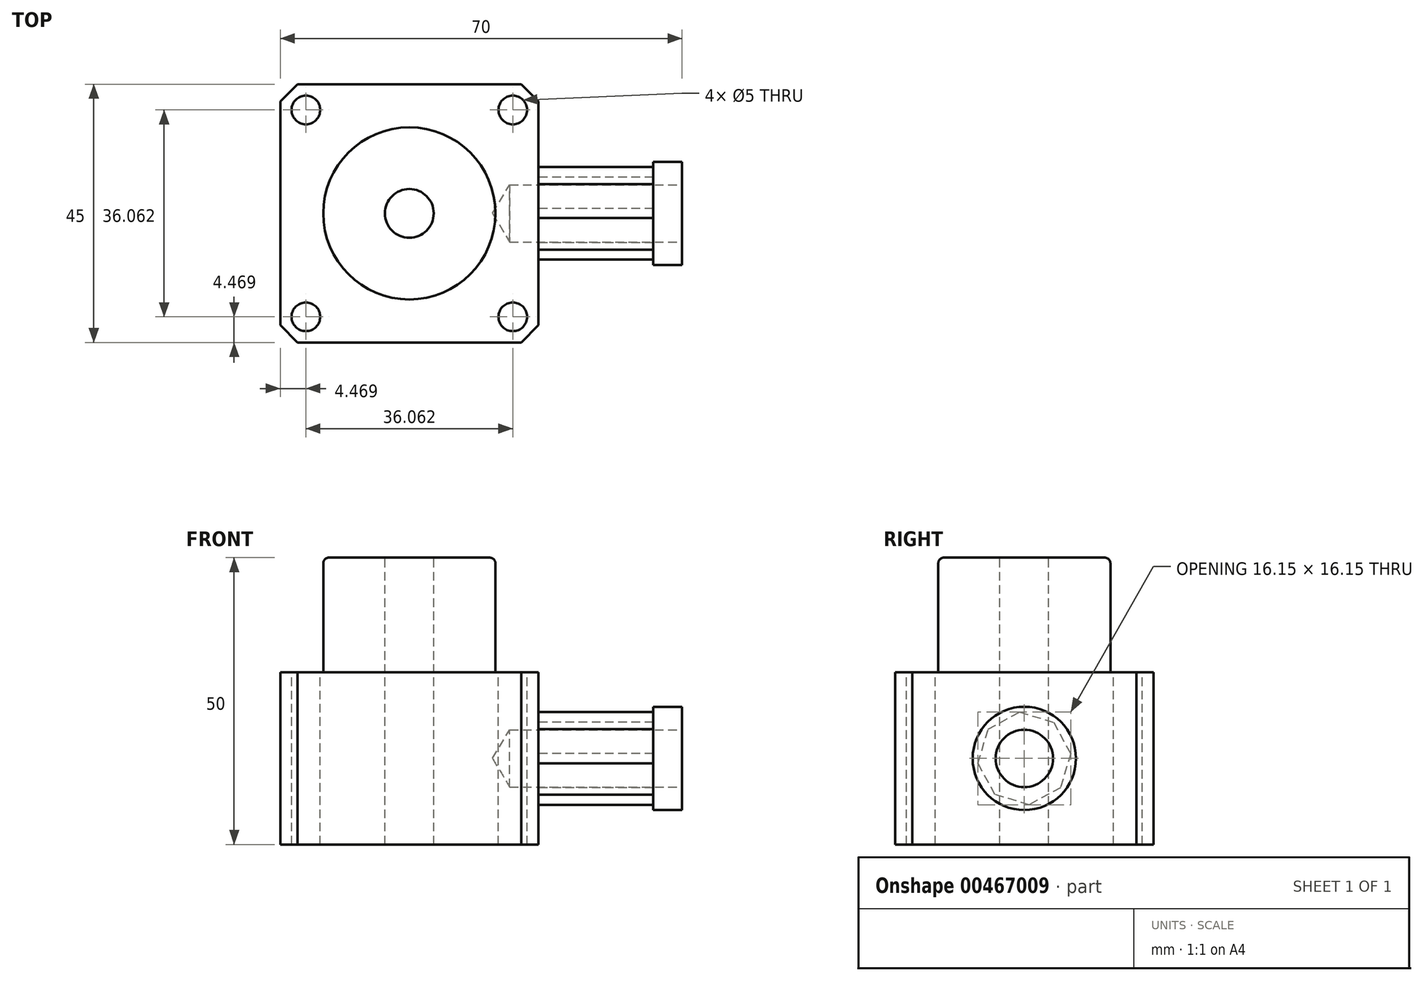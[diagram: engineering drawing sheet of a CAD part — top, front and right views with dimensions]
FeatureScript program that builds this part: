
annotation { "Feature Type Name" : "Feature", "Feature Type Description" : "" }
export const myFeature = defineFeature(function(context is Context, id is Id, definition is map)
    precondition{}
    {
        {
            var Q0;
            Q0=qCreatedBy(makeId("Top.planeOp"),FACE);
            var sketch = newSketch(context, id + "F0", { "sketchPlane" : qUnion([Q0])});
            skLineSegment(sketch, "E0.bottom", {"start": v(0, 0) * mm, "end": v(-45, 0) * mm});
            skLineSegment(sketch, "E0.top", {"start": v(0, -45) * mm, "end": v(-45, -45) * mm});
            skLineSegment(sketch, "E0.left", {"start": v(0, 0) * mm, "end": v(0, -45) * mm});
            skLineSegment(sketch, "E0.right", {"start": v(-45, 0) * mm, "end": v(-45, -45) * mm});
            skSolve(sketch);
        }
        {
            var Q0;
            Q0=makeQuery(id+"F0.imprint","IMPRINT",FACE,{"disambiguationData":[TD([[makeQuery(id+"F0.imprint","IMPRINT",EDGE,{"derivedFrom":sQuery(id+"F0.wireOp",EDGE,"E0.bottom")}),1.0]])]});
            extrude(context, id + "F1", {"entities" : qUnion([Q0]), "depth" : 30 * mm});
        }
        {
            var Q0;
            Q0=makeQuery(id+"F1.opExtrude","SWEPT_EDGE",EDGE,{"disambiguationData":[OSD([sQuery(id+"F0.wireOp",EDGE,"E0.top"),sQuery(id+"F0.wireOp",EDGE,"E0.right")])]});
            var Q1;
            Q1=makeQuery(id+"F1.opExtrude","SWEPT_EDGE",EDGE,{"disambiguationData":[OSD([sQuery(id+"F0.wireOp",EDGE,"E0.top"),sQuery(id+"F0.wireOp",EDGE,"E0.left")])]});
            var Q2;
            Q2=makeQuery(id+"F1.opExtrude","SWEPT_EDGE",EDGE,{"disambiguationData":[OSD([sQuery(id+"F0.wireOp",EDGE,"E0.bottom"),sQuery(id+"F0.wireOp",EDGE,"E0.left")])]});
            var Q3;
            Q3=makeQuery(id+"F1.opExtrude","SWEPT_EDGE",EDGE,{"disambiguationData":[OSD([sQuery(id+"F0.wireOp",EDGE,"E0.bottom"),sQuery(id+"F0.wireOp",EDGE,"E0.right")])]});
            chamfer(context, id + "F2", {"entities" : qUnion([Q0, Q1, Q2, Q3]), "width" : 3 * mm, "tangentPropagation" : true});
        }
        {
            var Q0;
            Q0=makeQuery(id+"F1.opExtrude","CAP_FACE",FACE,{"disambiguationData":[OSD([sQuery(id+"F0.wireOp",EDGE,"E0.bottom"),sQuery(id+"F0.wireOp",EDGE,"E0.top"),sQuery(id+"F0.wireOp",EDGE,"E0.left"),sQuery(id+"F0.wireOp",EDGE,"E0.right")])],"isStart":false});
            var sketch = newSketch(context, id + "F3", { "sketchPlane" : qUnion([Q0])});
            skLineSegment(sketch, "E1", {"start": v(-22.5, -22.5) * mm, "end": v(0, -22.5) * mm});
            skPoint(sketch, "E1.startSnap0", {"position": v(-22.5, -3) * mm});
            skPoint(sketch, "E1.startSnap1", {"position": v(0, -22.5) * mm});
            skLineSegment(sketch, "E2", {"start": v(0, -22.5) * mm, "end": v(-22.5, -22.5) * mm});
            skLineSegment(sketch, "E3", {"start": v(-22.5, -22.5) * mm, "end": v(-40.53, -40.53) * mm});
            skLineSegment(sketch, "E4.MirrorCS", {"start": v(-22.5, -22.5) * mm, "end": v(-40.53, -4.47) * mm});
            skPoint(sketch, "E5", {"position": v(-40.53, -40.53) * mm});
            skPoint(sketch, "E6", {"position": v(-40.53, -4.47) * mm});
            skLineSegment(sketch, "E7", {"start": v(-22.5, -22.5) * mm, "end": v(-4.47, -4.47) * mm});
            skLineSegment(sketch, "E8.MirrorCS", {"start": v(-22.5, -22.5) * mm, "end": v(-4.47, -40.53) * mm});
            skPoint(sketch, "E9", {"position": v(-4.47, -4.47) * mm});
            skPoint(sketch, "E10", {"position": v(-4.47, -40.53) * mm});
            skSolve(sketch);
        }
        {
            var Q0;
            Q0=sQuery(id+"F3.wireOp",VERTEX,"E5");
            var Q1;
            Q1=sQuery(id+"F3.wireOp",VERTEX,"E6");
            var Q2;
            Q2=sQuery(id+"F3.wireOp",VERTEX,"E9");
            var Q3;
            Q3=sQuery(id+"F3.wireOp",VERTEX,"E10");
            var Q4;
            Q4=makeQuery(id+"F1.opExtrude","SWEPT_BODY",BODY,{"disambiguationData":[OSD([sQuery(id+"F0.wireOp",EDGE,"E0.bottom"),sQuery(id+"F0.wireOp",EDGE,"E0.top"),sQuery(id+"F0.wireOp",EDGE,"E0.left"),sQuery(id+"F0.wireOp",EDGE,"E0.right")])]});
            hole(context, id + "F4", {"style" : HoleStyle.SIMPLE, "endStyle" : HoleEndStyle.THROUGH, "holeDiameter" : 5 * mm, "isTappedThrough" : true, "tappedDepth" : 12 * mm, "tapClearance" : 3, "locations" : qUnion([Q0, Q1, Q2, Q3]), "scope" : qUnion([Q4])});
        }
        {
            var Q0;
            Q0=makeQuery(id+"F1.opExtrude","SWEPT_FACE",FACE,{"disambiguationData":[OSD([sQuery(id+"F0.wireOp",EDGE,"E0.left")])]});
            var sketch = newSketch(context, id + "F5", { "sketchPlane" : qUnion([Q0])});
            skCircle(sketch, "E11", {"center": v(-22.5, 15) * mm, "radius": 7.5 * mm});
            skPoint(sketch, "E11.centerSnap0", {"position": v(-42, 15) * mm});
            skPoint(sketch, "E11.centerSnap1", {"position": v(-22.5, 30) * mm});
            skCircle(sketch, "E12.cCircle", {"center": v(-22.5, 15) * mm, "radius": 7.5 * mm, "construction": true});
            skLineSegment(sketch, "E12.0", {"start": v(-30.57, 14.16) * mm, "end": v(-28.8, 20.12) * mm});
            skLineSegment(sketch, "E12.1", {"start": v(-28.8, 20.12) * mm, "end": v(-23.34, 23.07) * mm});
            skLineSegment(sketch, "E12.2", {"start": v(-23.34, 23.07) * mm, "end": v(-17.38, 21.3) * mm});
            skLineSegment(sketch, "E12.3", {"start": v(-17.38, 21.3) * mm, "end": v(-14.43, 15.84) * mm});
            skLineSegment(sketch, "E12.4", {"start": v(-14.43, 15.84) * mm, "end": v(-16.2, 9.88) * mm});
            skLineSegment(sketch, "E12.5", {"start": v(-16.2, 9.88) * mm, "end": v(-21.66, 6.93) * mm});
            skLineSegment(sketch, "E12.6", {"start": v(-21.66, 6.93) * mm, "end": v(-27.62, 8.7) * mm});
            skLineSegment(sketch, "E12.7", {"start": v(-27.62, 8.7) * mm, "end": v(-30.57, 14.16) * mm});
            skPoint(sketch, "E12.0.midPoint", {"position": v(-29.69, 17.14) * mm});
            skSolve(sketch);
        }
        {
            var Q0;
            Q0=qSketchRegion(id+"F5",true);
            extrude(context, id + "F6", {"entities" : qUnion([Q0]), "operationType" : NewBodyOperationType.ADD, "depth" : 20 * mm});
        }
        {
            var Q0;
            Q0=makeQuery(id+"F6.opExtrude","CAP_FACE",FACE,{"disambiguationData":[OSD([sQuery(id+"F5.wireOp",EDGE,"E12.0"),sQuery(id+"F5.wireOp",EDGE,"E12.1"),sQuery(id+"F5.wireOp",EDGE,"E12.2"),sQuery(id+"F5.wireOp",EDGE,"E12.3"),sQuery(id+"F5.wireOp",EDGE,"E12.4"),sQuery(id+"F5.wireOp",EDGE,"E12.5"),sQuery(id+"F5.wireOp",EDGE,"E12.6"),sQuery(id+"F5.wireOp",EDGE,"E12.7")])],"isStart":false});
            var sketch = newSketch(context, id + "F7", { "sketchPlane" : qUnion([Q0])});
            skLineSegment(sketch, "E13", {"start": v(-20.36, 22.19) * mm, "end": v(-24.64, 7.81) * mm});
            skLineSegment(sketch, "E14", {"start": v(-24.64, 7.81) * mm, "end": v(-29.69, 17.14) * mm});
            skLineSegment(sketch, "E15", {"start": v(-29.69, 17.14) * mm, "end": v(-15.31, 12.86) * mm});
            skCircle(sketch, "E16", {"center": v(-22.5, 15) * mm, "radius": 9 * mm});
            skSolve(sketch);
        }
        {
            var Q0;
            Q0=qSketchRegion(id+"F7",true);
            var Q1;
            {var subQ0=sQuery(id+"F7.wireOp",EDGE,"E14");Q1=makeQuery(id+"F7.imprint","IMPRINT",FACE,{"disambiguationData":[TD([[makeQuery(id+"F7.imprint","IMPRINT",EDGE,{"derivedFrom":subQ0}),-1.0]])]});}
            extrude(context, id + "F8", {"entities" : qUnion([Q0, Q1]), "operationType" : NewBodyOperationType.ADD, "depth" : 5 * mm});
        }
        {
            var Q0;
            Q0=makeQuery(id+"F8.opExtrude","CAP_FACE",FACE,{"disambiguationData":[OSD([sQuery(id+"F7.wireOp",EDGE,"E16")])],"isStart":false});
            var sketch = newSketch(context, id + "F9", { "sketchPlane" : qUnion([Q0])});
            skPoint(sketch, "E17", {"position": v(-22.5, 15) * mm});
            skSolve(sketch);
        }
        {
            var Q0;
            Q0=sQuery(id+"F9.wireOp",VERTEX,"E17");
            var Q1;
            Q1=makeQuery(id+"F1.opExtrude","SWEPT_BODY",BODY,{"disambiguationData":[OSD([sQuery(id+"F0.wireOp",EDGE,"E0.bottom"),sQuery(id+"F0.wireOp",EDGE,"E0.top"),sQuery(id+"F0.wireOp",EDGE,"E0.left"),sQuery(id+"F0.wireOp",EDGE,"E0.right")])]});
            hole(context, id + "F10", {"style" : HoleStyle.SIMPLE, "endStyle" : HoleEndStyle.BLIND, "holeDiameter" : 10 * mm, "holeDepth" : 30 * mm, "isTappedThrough" : true, "tappedDepth" : 12 * mm, "tapClearance" : 3, "locations" : qUnion([Q0]), "scope" : qUnion([Q1])});
        }
        {
            var Q0;
            Q0=makeQuery(id+"F1.opExtrude","CAP_FACE",FACE,{"disambiguationData":[OSD([sQuery(id+"F0.wireOp",EDGE,"E0.bottom"),sQuery(id+"F0.wireOp",EDGE,"E0.top"),sQuery(id+"F0.wireOp",EDGE,"E0.left"),sQuery(id+"F0.wireOp",EDGE,"E0.right")])],"isStart":false});
            var sketch = newSketch(context, id + "F11", { "sketchPlane" : qUnion([Q0])});
            skCircle(sketch, "E18", {"center": v(-22.5, -22.5) * mm, "radius": 15 * mm});
            skPoint(sketch, "E18.centerSnap0", {"position": v(-45, -22.5) * mm});
            skPoint(sketch, "E18.centerSnap1", {"position": v(-22.5, 0) * mm});
            skSolve(sketch);
        }
        {
            var Q0;
            Q0=makeQuery(id+"F11.imprint","IMPRINT",FACE,{"disambiguationData":[TD([[makeQuery(id+"F11.imprint","IMPRINT",EDGE,{"derivedFrom":sQuery(id+"F11.wireOp",EDGE,"E18")}),1.0]])]});
            extrude(context, id + "F12", {"entities" : qUnion([Q0]), "operationType" : NewBodyOperationType.ADD, "depth" : 20 * mm, "offsetDistance" : 25 * mm});
        }
        {
            var Q0;
            Q0=makeQuery(id+"F12.opExtrude","CAP_EDGE",EDGE,{"disambiguationData":[OSD([sQuery(id+"F11.wireOp",EDGE,"E18")])],"isStart":false});
            fillet(context, id + "F13", {"entities" : qUnion([Q0]), "radius" : 1 * mm, "tangentPropagation" : true, "allowEdgeOverflow" : false});
        }
        {
            var Q0;
            Q0=makeQuery(id+"F12.opExtrude","CAP_FACE",FACE,{"disambiguationData":[OSD([sQuery(id+"F11.wireOp",EDGE,"E18")])],"isStart":false});
            var sketch = newSketch(context, id + "F14", { "sketchPlane" : qUnion([Q0])});
            skPoint(sketch, "E19", {"position": v(-22.5, -22.5) * mm});
            skSolve(sketch);
        }
        {
            var Q0;
            Q0=sQuery(id+"F14.wireOp",VERTEX,"E19");
            var Q1;
            Q1=makeQuery(id+"F1.opExtrude","SWEPT_BODY",BODY,{"disambiguationData":[OSD([sQuery(id+"F0.wireOp",EDGE,"E0.bottom"),sQuery(id+"F0.wireOp",EDGE,"E0.top"),sQuery(id+"F0.wireOp",EDGE,"E0.left"),sQuery(id+"F0.wireOp",EDGE,"E0.right")])]});
            hole(context, id + "F15", {"style" : HoleStyle.SIMPLE, "endStyle" : HoleEndStyle.THROUGH, "holeDiameter" : 8.5 * mm, "isTappedThrough" : true, "tappedDepth" : 12 * mm, "tapClearance" : 3, "locations" : qUnion([Q0]), "scope" : qUnion([Q1])});
        }
    });
